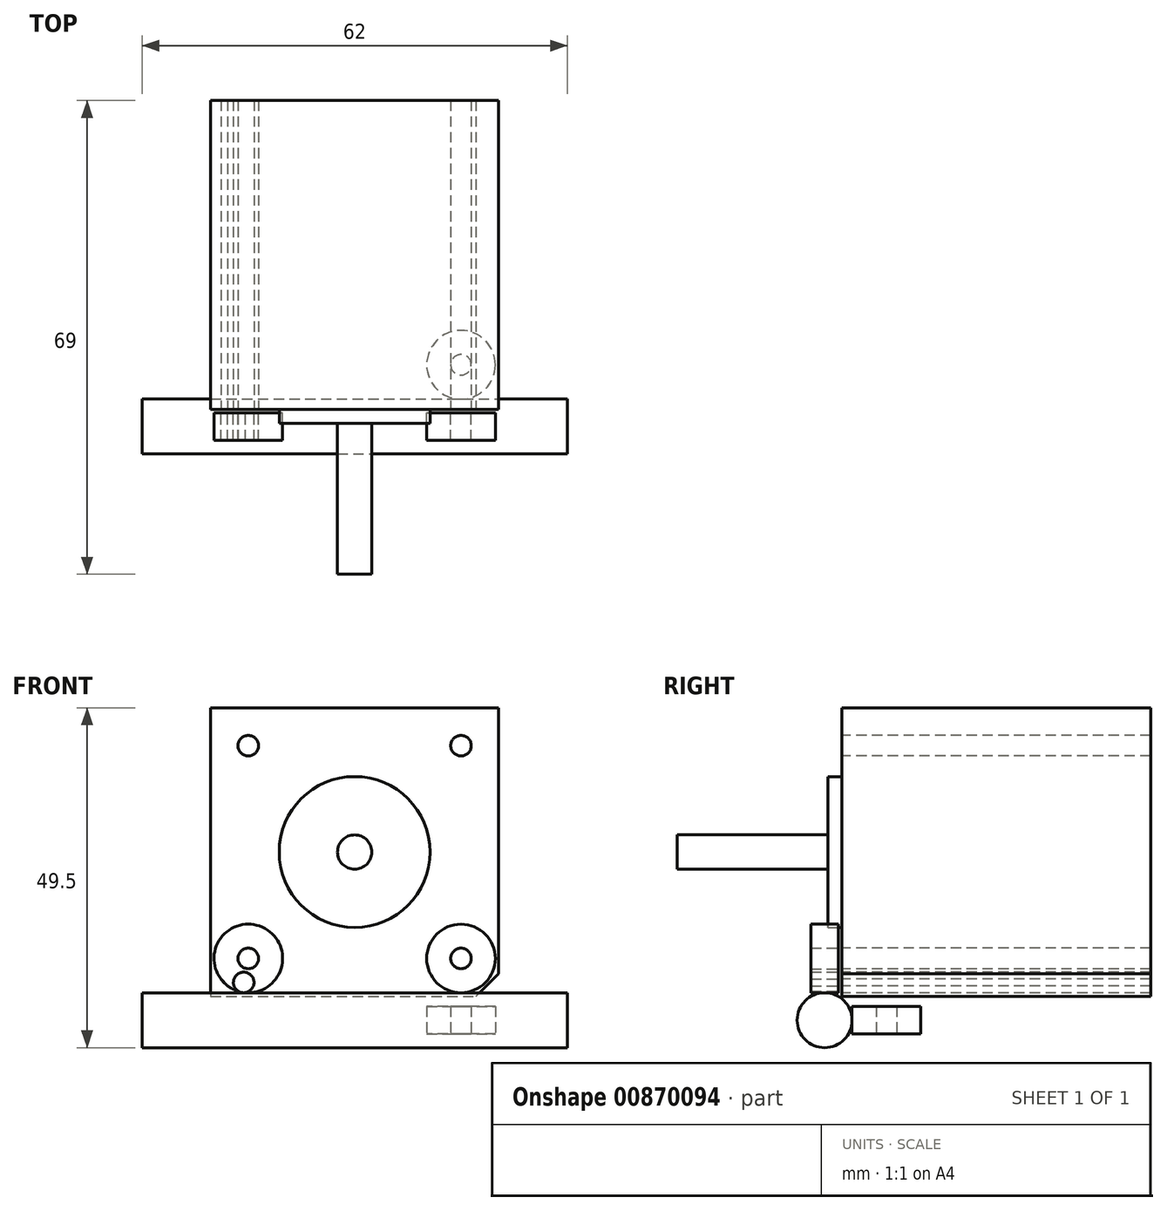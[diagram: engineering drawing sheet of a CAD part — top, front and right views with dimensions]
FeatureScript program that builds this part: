
annotation { "Feature Type Name" : "Feature", "Feature Type Description" : "" }
export const myFeature = defineFeature(function(context is Context, id is Id, definition is map)
    precondition{}
    {
        {
            var Q0;
            Q0=qCreatedBy(makeId("Front.planeOp"),FACE);
            var sketch = newSketch(context, id + "F0", { "sketchPlane" : qUnion([Q0])});
            skLineSegment(sketch, "E0.bottom", {"start": v(-21, 21) * mm, "end": v(21, 21) * mm});
            skLineSegment(sketch, "E0.top", {"start": v(-21, -21) * mm, "end": v(21, -21) * mm});
            skLineSegment(sketch, "E0.left", {"start": v(-21, 21) * mm, "end": v(-21, -21) * mm});
            skLineSegment(sketch, "E0.right", {"start": v(21, 21) * mm, "end": v(21, -21) * mm});
            skLineSegment(sketch, "E1", {"start": v(-37.86, 0) * mm, "end": v(37.86, 0) * mm, "construction": true});
            skLineSegment(sketch, "E2", {"start": v(0, -37.86) * mm, "end": v(0, 37.86) * mm, "construction": true});
            skCircle(sketch, "E3", {"center": v(-15.5, 15.5) * mm, "radius": 1.5 * mm});
            skCircle(sketch, "E4", {"center": v(-15.5, -15.5) * mm, "radius": 1.5 * mm});
            skCircle(sketch, "E5", {"center": v(15.5, 15.5) * mm, "radius": 1.5 * mm});
            skCircle(sketch, "E6", {"center": v(15.5, -15.5) * mm, "radius": 1.5 * mm});
            skCircle(sketch, "E7", {"center": v(0, 0) * mm, "radius": 2.5 * mm});
            skCircle(sketch, "E8", {"center": v(0, 0) * mm, "radius": 11 * mm});
            skCircle(sketch, "E9", {"center": v(-15.5, -15.5) * mm, "radius": 5 * mm});
            skCircle(sketch, "E10", {"center": v(15.5, -15.5) * mm, "radius": 5 * mm});
            skCircle(sketch, "E11", {"center": v(-16.17, -19) * mm, "radius": 1.5 * mm});
            skLineSegment(sketch, "E12", {"start": v(-21, -17) * mm, "end": v(-17, -21) * mm});
            skSolve(sketch);
        }
        {
            var Q0;
            Q0=makeQuery(id+"F0.imprint","IMPRINT",FACE,{"disambiguationData":[TD([[makeQuery(id+"F0.imprint","IMPRINT",EDGE,{"derivedFrom":sQuery(id+"F0.wireOp",EDGE,"E0.bottom")}),-1.0]])]});
            var Q1;
            Q1=makeQuery(id+"F0.imprint","IMPRINT",FACE,{"disambiguationData":[TD([[makeQuery(id+"F0.imprint","IMPRINT",EDGE,{"derivedFrom":sQuery(id+"F0.wireOp",EDGE,"E7")}),1.0]])]});
            var Q2;
            Q2=makeQuery(id+"F0.imprint","IMPRINT",FACE,{"disambiguationData":[TD([[makeQuery(id+"F0.imprint","IMPRINT",EDGE,{"derivedFrom":sQuery(id+"F0.wireOp",EDGE,"E7")}),-1.0]])]});
            var Q3;
            Q3=makeQuery(id+"F0.imprint","IMPRINT",FACE,{"disambiguationData":[TD([[makeQuery(id+"F0.imprint","IMPRINT",EDGE,{"derivedFrom":sQuery(id+"F0.wireOp",EDGE,"E4")}),-1.0]])]});
            var Q4;
            Q4=makeQuery(id+"F0.imprint","IMPRINT",FACE,{"disambiguationData":[TD([[makeQuery(id+"F0.imprint","IMPRINT",EDGE,{"derivedFrom":sQuery(id+"F0.wireOp",EDGE,"E6")}),-1.0]])]});
            var Q5;
            {var subQ0=sQuery(id+"F0.wireOp",EDGE,"E0.right");var subQ1=sQuery(id+"F0.wireOp",EDGE,"E0.top");var subQ2=makeQuery(id+"F0.imprint","INTERSECT",VERTEX,{"derivedFrom":[subQ1,subQ0]});Q5=makeQuery(id+"F0.imprint","IMPRINT",FACE,{"disambiguationData":[TD([[makeQuery(id+"F0.imprint","IMPRINT",EDGE,{"disambiguationData":[TD([[subQ2,1.0]])],"derivedFrom":subQ1}),1.0]])]});}
            var Q6;
            {var subQ0=sQuery(id+"F0.wireOp",EDGE,"E0.left");var subQ1=sQuery(id+"F0.wireOp",EDGE,"E0.top");var subQ2=makeQuery(id+"F0.imprint","INTERSECT",VERTEX,{"derivedFrom":[subQ1,subQ0]});Q6=makeQuery(id+"F0.imprint","IMPRINT",FACE,{"disambiguationData":[TD([[makeQuery(id+"F0.imprint","IMPRINT",EDGE,{"disambiguationData":[TD([[subQ2,-1.0]])],"derivedFrom":subQ1}),1.0]])]});}
            extrude(context, id + "F1", {"entities" : qUnion([Q0, Q1, Q2, Q3, Q4, Q5, Q6]), "oppositeDirection" : true, "depth" : 45 * mm, "offsetDistance" : 25 * mm});
        }
        {
            var Q0;
            Q0=makeQuery(id+"F0.imprint","IMPRINT",FACE,{"disambiguationData":[TD([[makeQuery(id+"F0.imprint","IMPRINT",EDGE,{"derivedFrom":sQuery(id+"F0.wireOp",EDGE,"E7")}),-1.0]])]});
            extrude(context, id + "F2", {"entities" : qUnion([Q0]), "operationType" : NewBodyOperationType.ADD, "depth" : 2 * mm, "offsetDistance" : 25 * mm});
        }
        {
            var Q0;
            Q0=makeQuery(id+"F0.imprint","IMPRINT",FACE,{"disambiguationData":[TD([[makeQuery(id+"F0.imprint","IMPRINT",EDGE,{"derivedFrom":sQuery(id+"F0.wireOp",EDGE,"E7")}),1.0]])]});
            extrude(context, id + "F3", {"entities" : qUnion([Q0]), "operationType" : NewBodyOperationType.ADD, "depth" : 24 * mm, "offsetDistance" : 25 * mm});
        }
        {
            var Q0;
            Q0=makeQuery(id+"F0.imprint","IMPRINT",FACE,{"disambiguationData":[TD([[makeQuery(id+"F0.imprint","IMPRINT",EDGE,{"derivedFrom":sQuery(id+"F0.wireOp",EDGE,"E4")}),-1.0]])]});
            var Q1;
            {var subQ0=sQuery(id+"F0.wireOp",EDGE,"E9");var subQ1=sQuery(id+"F0.wireOp",EDGE,"E0.left");var subQ2=makeQuery(id+"F0.imprint","INTERSECT",VERTEX,{"disambiguationData":[OD(0.0)],"derivedFrom":[subQ1,subQ0]});Q1=makeQuery(id+"F0.imprint","IMPRINT",FACE,{"disambiguationData":[TD([[makeQuery(id+"F0.imprint","IMPRINT",EDGE,{"disambiguationData":[TD([[subQ2,-1.0]])],"derivedFrom":subQ1}),-1.0]])]});}
            var Q2;
            {var subQ0=sQuery(id+"F0.wireOp",EDGE,"E9");var subQ1=sQuery(id+"F0.wireOp",EDGE,"E0.top");var subQ2=makeQuery(id+"F0.imprint","INTERSECT",VERTEX,{"disambiguationData":[OD(0.0)],"derivedFrom":[subQ1,subQ0]});Q2=makeQuery(id+"F0.imprint","IMPRINT",FACE,{"disambiguationData":[TD([[makeQuery(id+"F0.imprint","IMPRINT",EDGE,{"disambiguationData":[TD([[subQ2,-1.0]])],"derivedFrom":subQ1}),-1.0]])]});}
            var Q3;
            {var subQ0=sQuery(id+"F0.wireOp",EDGE,"E10");var subQ1=sQuery(id+"F0.wireOp",EDGE,"E0.right");var subQ2=makeQuery(id+"F0.imprint","INTERSECT",VERTEX,{"disambiguationData":[OD(0.0)],"derivedFrom":[subQ1,subQ0]});Q3=makeQuery(id+"F0.imprint","IMPRINT",FACE,{"disambiguationData":[TD([[makeQuery(id+"F0.imprint","IMPRINT",EDGE,{"disambiguationData":[TD([[subQ2,-1.0]])],"derivedFrom":subQ1}),1.0]])]});}
            var Q4;
            Q4=makeQuery(id+"F0.imprint","IMPRINT",FACE,{"disambiguationData":[TD([[makeQuery(id+"F0.imprint","IMPRINT",EDGE,{"derivedFrom":sQuery(id+"F0.wireOp",EDGE,"E6")}),-1.0]])]});
            var Q5;
            {var subQ0=sQuery(id+"F0.wireOp",EDGE,"E10");var subQ1=sQuery(id+"F0.wireOp",EDGE,"E0.top");var subQ2=makeQuery(id+"F0.imprint","INTERSECT",VERTEX,{"disambiguationData":[OD(0.0)],"derivedFrom":[subQ1,subQ0]});Q5=makeQuery(id+"F0.imprint","IMPRINT",FACE,{"disambiguationData":[TD([[makeQuery(id+"F0.imprint","IMPRINT",EDGE,{"disambiguationData":[TD([[subQ2,-1.0]])],"derivedFrom":subQ1}),-1.0]])]});}
            extrude(context, id + "F4", {"entities" : qUnion([Q0, Q1, Q2, Q3, Q4, Q5]), "depth" : 4.5 * mm, "offsetDistance" : 25 * mm, "hasSecondDirection" : true, "secondDirectionOppositeDirection" : true, "secondDirectionDepth" : -.5 * mm});
        }
        {
            var Q0;
            Q0=makeQuery(id+"F1.opExtrude","SWEPT_FACE",FACE,{"disambiguationData":[OSD([sQuery(id+"F0.wireOp",EDGE,"E0.right")])]});
            var sketch = newSketch(context, id + "F5", { "sketchPlane" : qUnion([Q0])});
            skLineSegment(sketch, "E13", {"start": v(-2.5, -17.83) * mm, "end": v(-2.5, -31.17) * mm, "construction": true});
            skLineSegment(sketch, "E14", {"start": v(-9.17, -24.5) * mm, "end": v(4.17, -24.5) * mm, "construction": true});
            skCircle(sketch, "E15", {"center": v(-2.5, -24.5) * mm, "radius": 4 * mm});
            skLineSegment(sketch, "E16", {"start": v(-1, -20.5) * mm, "end": v(-7, -20.5) * mm, "construction": true});
            skLineSegment(sketch, "E17.0.0", {"start": v(-4.5, -20.5) * mm, "end": v(-4.5, -10.5) * mm, "construction": true});
            skLineSegment(sketch, "E18.0.0", {"start": v(-0.5, -10.5) * mm, "end": v(-0.5, -20.5) * mm, "construction": true});
            skSolve(sketch);
        }
        {
            var Q0;
            Q0=makeQuery(id+"F5.imprint","IMPRINT",FACE,{"disambiguationData":[TD([[makeQuery(id+"F5.imprint","IMPRINT",EDGE,{"derivedFrom":sQuery(id+"F5.wireOp",EDGE,"E15")}),1.0]])]});
            extrude(context, id + "F6", {"entities" : qUnion([Q0]), "oppositeDirection" : true, "depth" : 52 * mm, "offsetDistance" : 25 * mm, "hasSecondDirection" : true, "secondDirectionOppositeDirection" : true, "secondDirectionDepth" : -10 * mm});
        }
        {
            var Q0;
            Q0=makeQuery(id+"F4.opExtrude","SWEPT_BODY",BODY,{"disambiguationData":[OSD([sQuery(id+"F0.wireOp",EDGE,"E6"),sQuery(id+"F0.wireOp",EDGE,"E10")])]});
            var Q1;
            Q1=makeQuery(id+"F6.opExtrude","SWEPT_FACE",FACE,{"disambiguationData":[OSD([sQuery(id+"F5.wireOp",EDGE,"E15")])]});
            transform(context, id + "F7", {"entities" : qUnion([Q0]), "transformType" : TransformType.ROTATION, "transformAxis" : qUnion([Q1]), "angle" : 90 * degree, "oppositeDirection" : true, "makeCopy" : true});
        }
        {
            var Q0;
            Q0=makeQuery(id+"F1.opExtrude","SWEPT_EDGE",EDGE,{"disambiguationData":[OSD([sQuery(id+"F0.wireOp",EDGE,"E0.top"),sQuery(id+"F0.wireOp",EDGE,"E0.right")])]});
            chamfer(context, id + "F8", {"entities" : qUnion([Q0]), "width" : 3.3 * mm, "tangentPropagation" : true});
        }
    });
